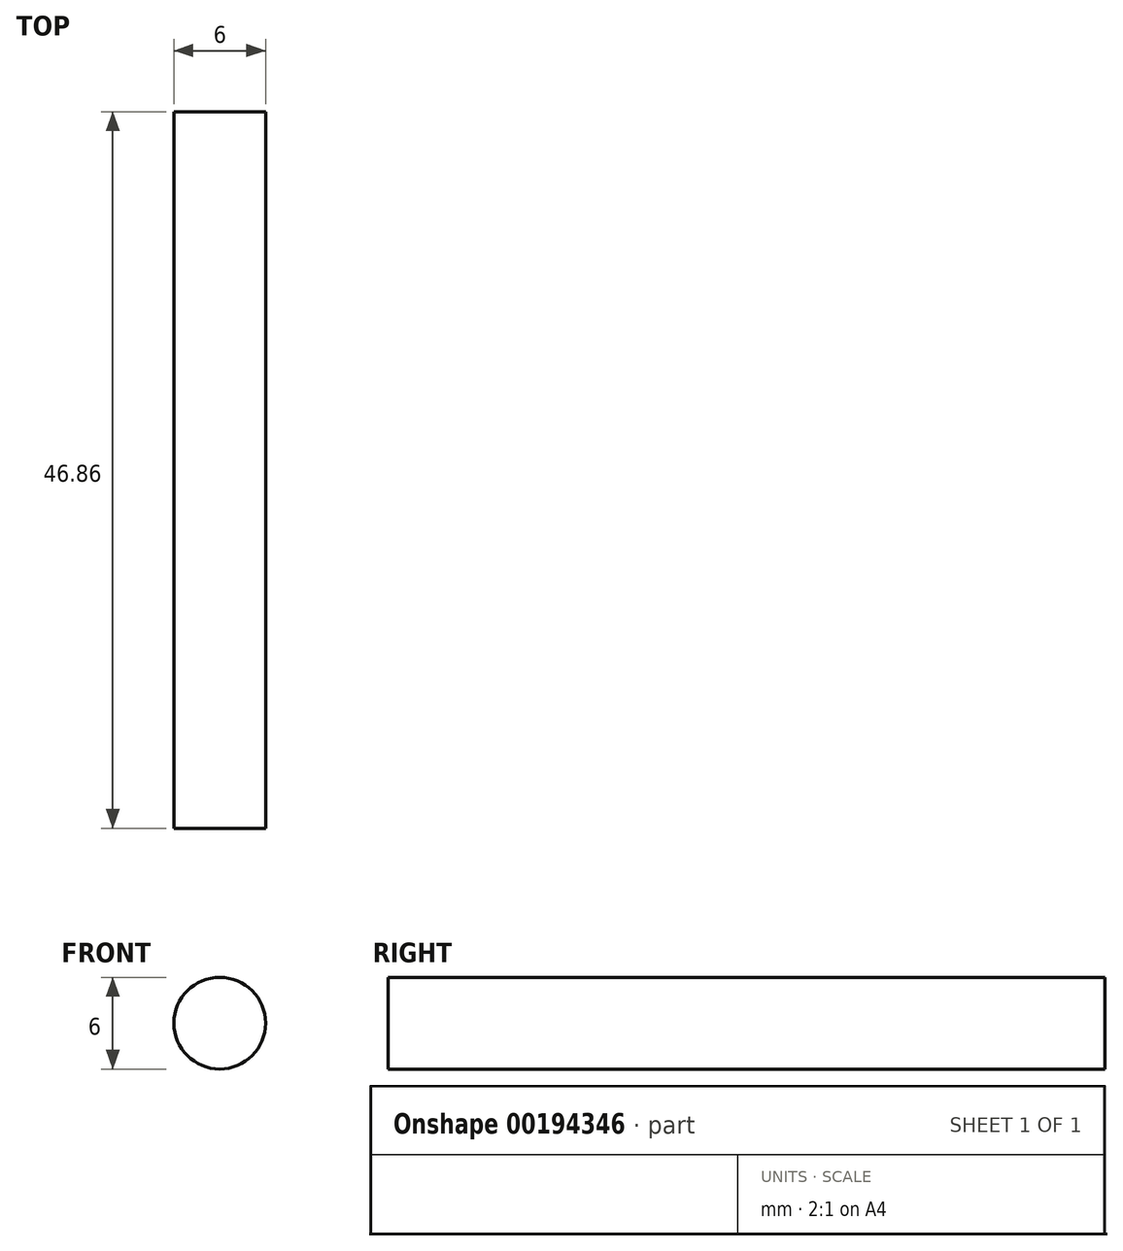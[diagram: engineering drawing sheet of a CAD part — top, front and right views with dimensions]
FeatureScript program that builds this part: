
annotation { "Feature Type Name" : "Feature", "Feature Type Description" : "" }
export const myFeature = defineFeature(function(context is Context, id is Id, definition is map)
    precondition{}
    {
        {
            var Q0;
            Q0=qCreatedBy(makeId("Front.planeOp"),FACE);
            var sketch = newSketch(context, id + "F0", { "sketchPlane" : qUnion([Q0])});
            skCircle(sketch, "E0", {"center": v(0, 0) * mm, "radius": 3 * mm});
            skSolve(sketch);
        }
        {
            var Q0;
            Q0=qSketchRegion(id+"F0",true);
            extrude(context, id + "F1", {"entities" : qUnion([Q0]), "depth" : 46.86 * mm});
        }
    });
